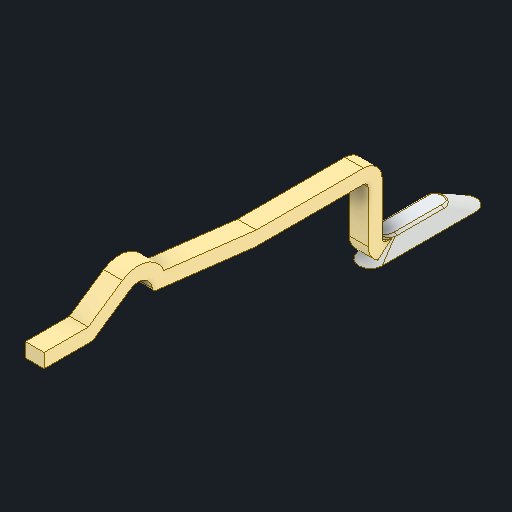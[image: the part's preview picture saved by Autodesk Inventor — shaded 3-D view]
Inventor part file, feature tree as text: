
AUTODESK INVENTOR PART (.ipt)
format: ipt  version: 2023 (Build 270158000, 158)  size: 157,696 bytes
history: native  units: in
note: dims shown in document units (in); Inventor stores cm internally (conversion verified against a paired STEP export)
features: fillet x1
ambient origin geometry x8: Origin, YZ Plane, XZ Plane, XY Plane, X Axis, Y Axis, Z Axis, Center Point
bodies: Solid1 (feature_tree)
feature tree (1):
  fillet  "Fillet2"  [1 undecoded]
note: 1 required parameter value undecoded (feature->parameter linkage not recoverable at this tier; creation-order binding heuristic only, values carry confidence <= 0.55)
